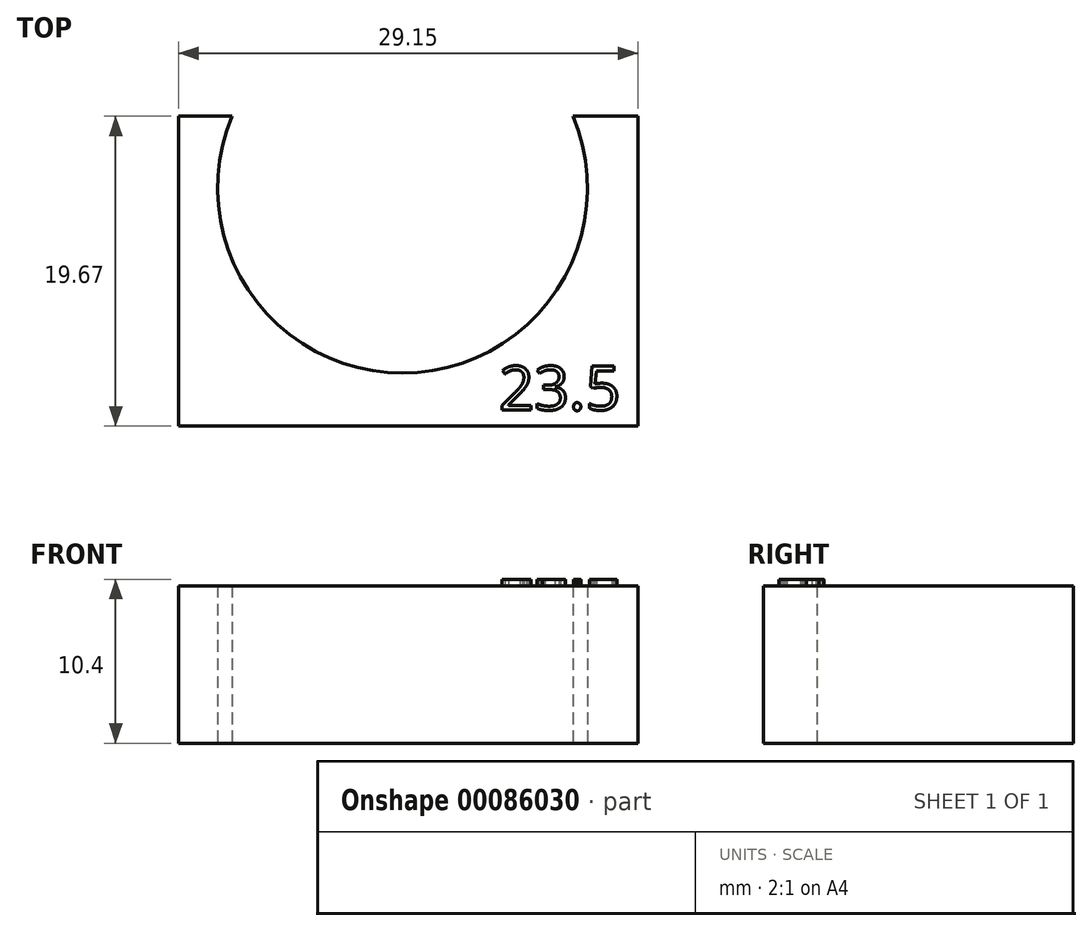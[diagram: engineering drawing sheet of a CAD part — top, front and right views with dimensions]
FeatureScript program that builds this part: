
annotation { "Feature Type Name" : "Feature", "Feature Type Description" : "" }
export const myFeature = defineFeature(function(context is Context, id is Id, definition is map)
    precondition{}
    {
        {
            var Q0;
            Q0=qCreatedBy(makeId("Top.planeOp"),FACE);
            var sketch = newSketch(context, id + "F0", { "sketchPlane" : qUnion([Q0])});
            skCircle(sketch, "E0", {"center": v(0, 0) * mm, "radius": 11.75 * mm});
            skLineSegment(sketch, "E1.bottom", {"start": v(-14.21, 4.55) * mm, "end": v(14.94, 4.55) * mm});
            skLineSegment(sketch, "E1.top", {"start": v(-14.21, -15.12) * mm, "end": v(14.94, -15.12) * mm});
            skLineSegment(sketch, "E1.left", {"start": v(-14.21, 4.55) * mm, "end": v(-14.21, -15.12) * mm});
            skLineSegment(sketch, "E1.right", {"start": v(14.94, 4.55) * mm, "end": v(14.94, -15.12) * mm});
            skSolve(sketch);
        }
        {
            var Q0;
            Q0=makeQuery(id+"F0.imprint","IMPRINT",FACE,{"disambiguationData":[TD([[makeQuery(id+"F0.imprint","IMPRINT",EDGE,{"derivedFrom":sQuery(id+"F0.wireOp",EDGE,"E0")}),-1.0]])]});
            extrude(context, id + "F1", {"entities" : qUnion([Q0]), "depth" : 10 * mm});
        }
        {
            var Q0;
            Q0=makeQuery(id+"F1.opExtrude","SWEPT_BODY",BODY,{"disambiguationData":[OSD([sQuery(id+"F0.wireOp",EDGE,"E0"),sQuery(id+"F0.wireOp",EDGE,"E1.bottom"),sQuery(id+"F0.wireOp",EDGE,"E1.top"),sQuery(id+"F0.wireOp",EDGE,"E1.left"),sQuery(id+"F0.wireOp",EDGE,"E1.right")])]});
            transform(context, id + "F2", {"entities" : qUnion([Q0]), "transformType" : TransformType.TRANSLATION_3D, "dx" : 0 * mm, "dy" : 0 * mm, "dz" : 0 * mm, "makeCopy" : true});
        }
        {
            var Q0;
            Q0=makeQuery(id+"F2.opPattern","COPY",BODY,{"derivedFrom":makeQuery(id+"F1.opExtrude","SWEPT_BODY",BODY,{"disambiguationData":[OSD([sQuery(id+"F0.wireOp",EDGE,"E0"),sQuery(id+"F0.wireOp",EDGE,"E1.bottom"),sQuery(id+"F0.wireOp",EDGE,"E1.top"),sQuery(id+"F0.wireOp",EDGE,"E1.left"),sQuery(id+"F0.wireOp",EDGE,"E1.right")])]}),"instanceName":"1"});
            deleteBodies(context, id + "F3", {"entities" : qUnion([Q0])});
        }
        {
            var Q0;
            Q0=makeQuery(id+"F1.opExtrude","CAP_FACE",FACE,{"disambiguationData":[OSD([sQuery(id+"F0.wireOp",EDGE,"E0"),sQuery(id+"F0.wireOp",EDGE,"E1.bottom"),sQuery(id+"F0.wireOp",EDGE,"E1.top"),sQuery(id+"F0.wireOp",EDGE,"E1.left"),sQuery(id+"F0.wireOp",EDGE,"E1.right")])],"isStart":false});
            var sketch = newSketch(context, id + "F4", { "sketchPlane" : qUnion([Q0])});
            skText(sketch, "E2", { "text": "23.5", "fontName": "OpenSans-Regular.ttf"});
            const initialGuessF4  = {"E2": [0.00613, -0.0141, 1, 0, 0.0028]};
            skSetInitialGuess(sketch, initialGuessF4);
            skSolve(sketch);
        }
        {
            var Q0;
            Q0 = qSketchRegion(id + "F4", true);
            extrude(context, id + "F5", {"entities" : qUnion([Q0]), "operationType" : NewBodyOperationType.ADD, "depth" : .4 * mm});
        }
    });
